# Revit family: GR_Адаптер линейный_Муфта(1)_VL-S-КСД-У-О_R21
name_source: partatom
category: Соединительные детали воздуховодов
units: mm (PartAtom-declared; Revit-internal decimal feet)

## family parameters
Всегда вертикально = Да
Заголовок OmniClass = Metal Ducts
На основе рабочей плоскости = Нет
Номер OmniClass = 23.75.70.14.31
Общий = Нет
При загрузке вырезать с полостями = Нет
Размер круглого соединителя = Использовать диаметр
Тип детали = Мультипорт

## types (15) — shared parameters
ADSK_URL страницы изделия = https://grilles.ru
ADSK_Версия Revit = 2021
ADSK_Единица измерения = шт.
ADSK_Завод-изготовитель = ООО "ВЕНТРЕШЕТКИКОМ"
ADSK_Код изделия = 00159
ADSK_Количество = 1
ADSK_Материал = ADSK_Оцинкованная сталь
ADSK_Наименование = VL-S-КСД-У-О, адаптер вентиляционной решётки
Изготовитель = ООО "ВЕНТРЕШЕТКИКОМ"
Корпус_Металл_Толщина = 1 мм
Муфта_Металл_Толщина = 1 мм
zero-valued in all types: Отметка по умолчанию

## per-type parameters (varying)
| type | Корпус_Высота | Корпус_Длина | Решетка_отступ | Решётка_Высота |
| VL-S-КСД-У-О 1-20 | 130 мм | 170 мм | 26 мм | 50 мм |
| VL-S-КСД-У-О 1-30 | 130 мм | 180 мм | 31 мм | 60 мм |
| VL-S-КСД-У-О 1-40 | 130 мм | 190 мм | 36 мм | 70 мм |
| VL-S-КСД-У-О 1-50 | 130 мм | 200 мм | 41 мм | 80 мм |
| VL-S-КСД-У-О 1-60 | 170 мм | 210 мм | 46 мм | 90 мм |
| VL-S-КСД-У-О 1-70 | 170 мм | 220 мм | 51 мм | 100 мм |
| VL-S-КСД-У-О 2-20 | 130 мм | 210 мм | 46 мм | 90 мм |
| VL-S-КСД-У-О 2-25 | 130 мм | 220 мм | 51 мм | 100 мм |
| VL-S-КСД-У-О 2-30 | 130 мм | 230 мм | 56 мм | 110 мм |
| VL-S-КСД-У-О 3-20 | 130 мм | 250 мм | 66 мм | 130 мм |
| VL-S-КСД-У-О 3-25 | 130 мм | 265 мм | 74 мм | 145 мм |
| VL-S-КСД-У-О 3-30 | 130 мм | 280 мм | 81 мм | 160 мм |
| VL-S-КСД-У-О 4-20 | 170 мм | 290 мм | 86 мм | 170 мм |
| VL-S-КСД-У-О 4-25 | 170 мм | 310 мм | 96 мм | 190 мм |
| VL-S-КСД-У-О 4-30 | 170 мм | 330 мм | 106 мм | 210 мм |

note: column(s) folded — value = type name in every type: ADSK_Марка
